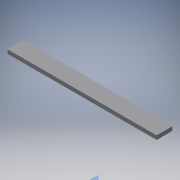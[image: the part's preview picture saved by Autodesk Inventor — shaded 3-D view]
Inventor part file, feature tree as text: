
AUTODESK INVENTOR PART (.ipt)
format: ipt  version: 2018.2 (Build 222227000, 227)  size: 97,280 bytes
history: native  units: in
note: dims shown in document units (in); Inventor stores cm internally (conversion verified against a paired STEP export)
features: other x3, extrude x1, sketch x1, reference x1
ambient origin geometry x8: Origin, YZ Plane, XZ Plane, XY Plane, X Axis, Y Axis, Z Axis, Center Point
bodies: Solid1 (feature_tree)
feature tree (6):
  extrude  "Extrusion1"  Depth=27.476in
  sketch  "Sketch1"  dims[d0=0.75in d1=27.476in d2=3.0in d3=0.0in]
  reference  "Reference1"
  parser-record x1  (decoder bookkeeping rows leaked as tree rows — omitted from the tree; the rows remain in map.json)
  other  "Mounting Part figureing outness.iam"
  other  "Wheel mounting side part:1"
note: 1 file-system path scrubbed to <path> (originals preserved in map.json)
